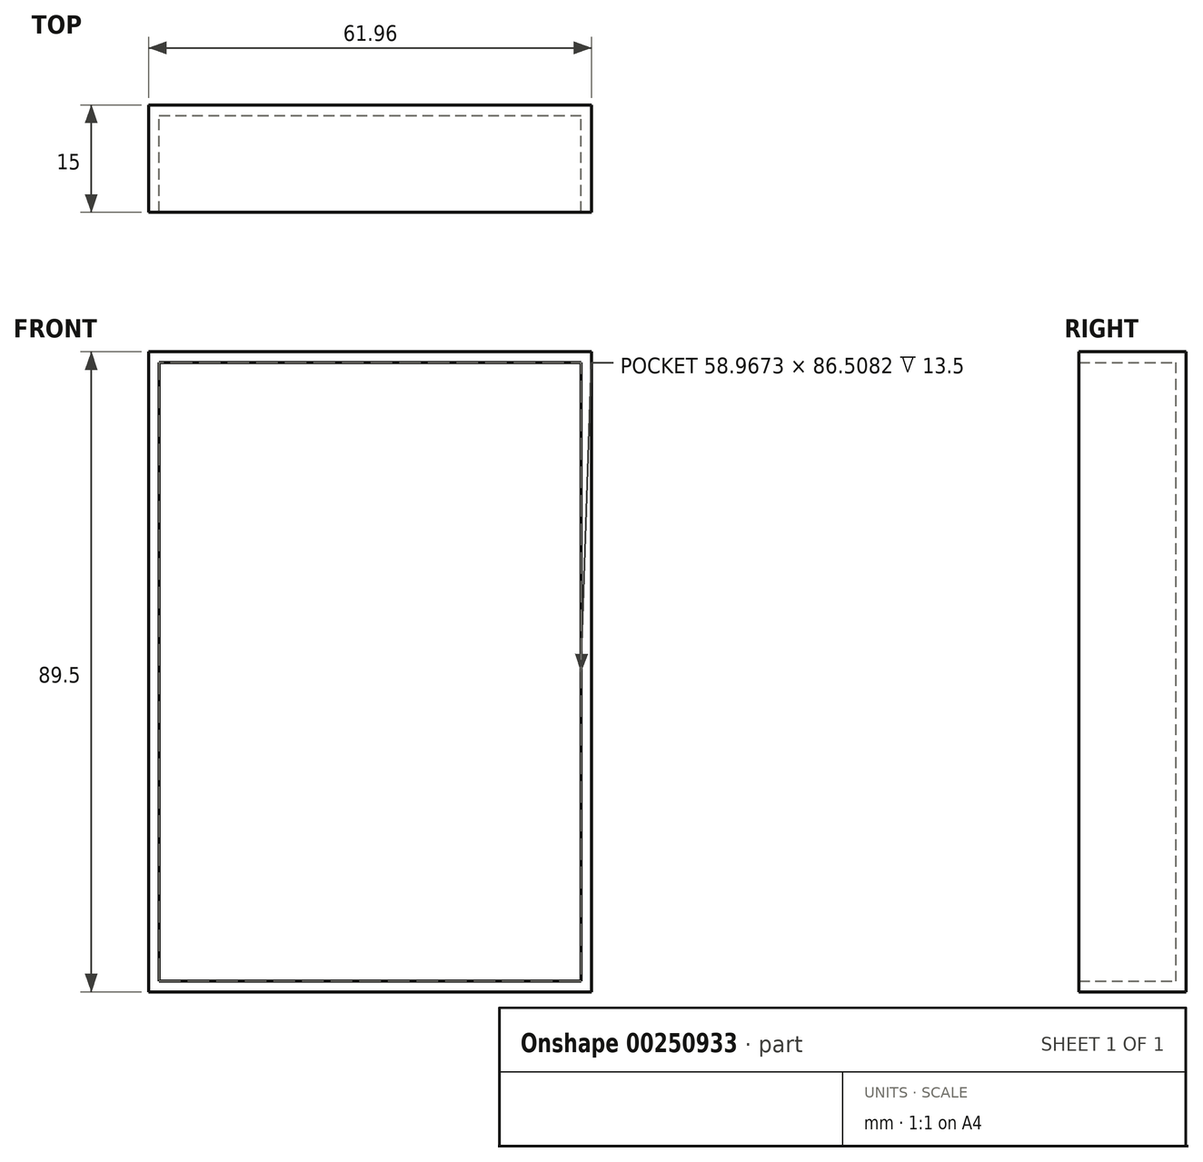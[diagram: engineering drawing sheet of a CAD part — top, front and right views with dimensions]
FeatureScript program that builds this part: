
annotation { "Feature Type Name" : "Feature", "Feature Type Description" : "" }
export const myFeature = defineFeature(function(context is Context, id is Id, definition is map)
    precondition{}
    {
        {
            var Q0;
            Q0=qCreatedBy(makeId("Front.planeOp"),FACE);
            var sketch = newSketch(context, id + "F0", { "sketchPlane" : qUnion([Q0])});
            skLineSegment(sketch, "E0.bottom", {"start": v(-28.11, 57.23) * mm, "end": v(33.85, 57.23) * mm});
            skLineSegment(sketch, "E0.top", {"start": v(-28.11, -32.27) * mm, "end": v(33.85, -32.27) * mm});
            skLineSegment(sketch, "E0.left", {"start": v(-28.11, 57.23) * mm, "end": v(-28.11, -32.27) * mm});
            skLineSegment(sketch, "E0.right", {"start": v(33.85, 57.23) * mm, "end": v(33.85, -32.27) * mm});
            skSolve(sketch);
        }
        {
            var Q0;
            Q0=makeQuery(id+"F0.imprint","IMPRINT",FACE,{"disambiguationData":[TD([[makeQuery(id+"F0.imprint","IMPRINT",EDGE,{"derivedFrom":sQuery(id+"F0.wireOp",EDGE,"E0.bottom")}),-1.0]])]});
            extrude(context, id + "F1", {"entities" : qUnion([Q0]), "endBound" : BoundingType.SYMMETRIC, "depth" : 15 * mm});
        }
        {
            var Q0;
            Q0=makeQuery(id+"F1.opExtrude","CAP_FACE",FACE,{"disambiguationData":[OSD([sQuery(id+"F0.wireOp",EDGE,"E0.bottom"),sQuery(id+"F0.wireOp",EDGE,"E0.top"),sQuery(id+"F0.wireOp",EDGE,"E0.left"),sQuery(id+"F0.wireOp",EDGE,"E0.right")])],"isStart":false});
            shell(context, id + "F2", {"entities" : qUnion([Q0]), "thickness" : 1.5 * mm});
        }
    });
